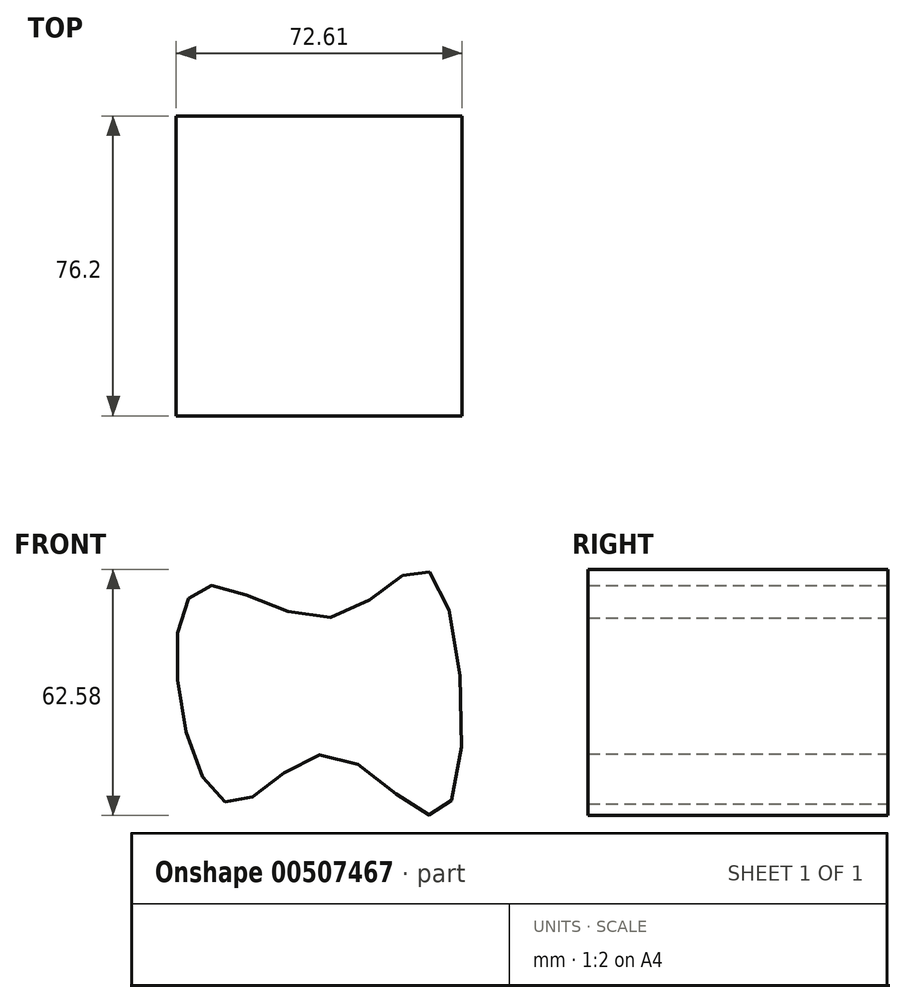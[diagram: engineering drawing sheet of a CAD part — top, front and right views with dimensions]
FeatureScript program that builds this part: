
annotation { "Feature Type Name" : "Feature", "Feature Type Description" : "" }
export const myFeature = defineFeature(function(context is Context, id is Id, definition is map)
    precondition{}
    {
        {
            var Q0;
            Q0=qCreatedBy(makeId("Front.planeOp"),FACE);
            var sketch = newSketch(context, id + "F0", { "sketchPlane" : qUnion([Q0])});
            skFitSpline(sketch, "E0", {"points": [v(-30.5, 11.52) * mm, v(-23.03, 35.44) * mm, v(9.87, 27.67) * mm, v(33.8, 38.73) * mm, v(36.79, -22.28) * mm, v(8.67, -7.33) * mm, v(-16.15, -19.9) * mm, v(-30.5, 11.52) * mm]});
            skSolve(sketch);
        }
        {
            var Q0;
            Q0=makeQuery(id+"F0.imprint","IMPRINT",FACE,{"disambiguationData":[TD([[makeQuery(id+"F0.imprint","IMPRINT",EDGE,{"derivedFrom":sQuery(id+"F0.wireOp",EDGE,"E0")}),-1.0]])]});
            var Q1;
            Q1=sQuery(id+"F0.wireOp",EDGE,"E0");
            extrude(context, id + "F1", {"entities" : qUnion([Q0]), "surfaceEntities" : qUnion([Q1]), "endBound" : BoundingType.SYMMETRIC, "depth" : 76.2 * mm});
        }
        {
            var Q0;
            Q0=makeQuery(id+"F1.opExtrude","CAP_FACE",FACE,{"disambiguationData":[OSD([sQuery(id+"F0.wireOp",EDGE,"E0")])],"isStart":true});
            cPlane(context, id + "F2", {"entities" : qUnion([Q0]), "cplaneType" : CPlaneType.OFFSET, "offset" : 76.2 * mm, "width" : 152.4 * mm, "height" : 152.4 * mm});
        }
        {
            var Q0;
            Q0=qCreatedBy(id+"F2.planeOp",FACE);
            var sketch = newSketch(context, id + "F3", { "sketchPlane" : qUnion([Q0])});
            skCircle(sketch, "E1.cCircle", {"center": v(-15.5, 0) * mm, "radius": 34.8 * mm, "construction": true});
            skLineSegment(sketch, "E1.0", {"start": v(19.9, 19.02) * mm, "end": v(18.68, -21.15) * mm});
            skLineSegment(sketch, "E1.1", {"start": v(18.68, -21.15) * mm, "end": v(-16.72, -40.17) * mm});
            skLineSegment(sketch, "E1.2", {"start": v(-16.72, -40.17) * mm, "end": v(-50.9, -19.02) * mm});
            skLineSegment(sketch, "E1.3", {"start": v(-50.9, -19.02) * mm, "end": v(-49.67, 21.15) * mm});
            skLineSegment(sketch, "E1.4", {"start": v(-49.67, 21.15) * mm, "end": v(-14.27, 40.17) * mm});
            skLineSegment(sketch, "E1.5", {"start": v(-14.27, 40.17) * mm, "end": v(19.9, 19.02) * mm});
            skPoint(sketch, "E1.0.midPoint", {"position": v(19.3, -1.06) * mm});
            skSolve(sketch);
        }
        {
            var Q0;
            Q0=makeQuery(id+"F1.opExtrude","CAP_FACE",FACE,{"disambiguationData":[OSD([sQuery(id+"F0.wireOp",EDGE,"E0")])],"isStart":true});
            var Q1;
            Q1=makeQuery(id+"F3.imprint","IMPRINT",FACE,{"disambiguationData":[TD([[makeQuery(id+"F3.imprint","IMPRINT",EDGE,{"derivedFrom":sQuery(id+"F3.wireOp",EDGE,"E1.0")}),-1.0]])]});
            var Q2;
            Q2=makeQuery(id+"F1.opExtrude","CAP_FACE",FACE,{"disambiguationData":[OSD([sQuery(id+"F0.wireOp",EDGE,"E0")])],"isStart":true});
            var Q3;
            Q3=makeQuery(id+"F3.imprint","IMPRINT",FACE,{"disambiguationData":[TD([[makeQuery(id+"F3.imprint","IMPRINT",EDGE,{"derivedFrom":sQuery(id+"F3.wireOp",EDGE,"E1.0")}),-1.0]])]});
            loft(context, id + "F4", {"bodyType" : ToolBodyType.SURFACE, "sheetProfilesArray" : [{ "sheetProfileEntities" : qUnion([Q0]) }, { "sheetProfileEntities" : qUnion([Q1]) }], "wireProfilesArray" : [{ "wireProfileEntities" : qUnion([Q2]) }, { "wireProfileEntities" : qUnion([Q3]) }]});
        }
    });
